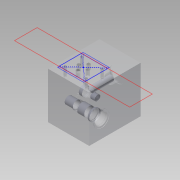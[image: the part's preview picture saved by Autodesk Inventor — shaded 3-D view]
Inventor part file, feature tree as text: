
AUTODESK INVENTOR PART (.ipt)
format: ipt  version: 2014 (Build 180170000, 170)  size: 423,424 bytes
history: native  units: mm
features: other x63, sketch x14, extrude x1
ambient origin geometry x8: Origin, YZ Plane, XZ Plane, XY Plane, X Axis, Y Axis, Z Axis, Center Point
bodies: 实体1 (feature_tree)
feature tree (78):
  other  "NULLNET"
  extrude  "拉伸1"  TaperAngle=0.0deg  [1 undecoded]
  other  "UCS1"
  other  "UCS2"
  other  "UCS3"
  other  "UCS4"
  other  "UCS5"
  other  "UCS6"
  other  "Footprint1"
  other  "Outline1"
  sketch  "草图1"  dims[d0=90.0mm d1=0.0mm]
  sketch  "草图5"  dims[d14=0.0mm d15=0.0mm d16=0.0mm d17=0.0mm d18=0.0mm d19=0.0mm]
  other  "曲面1"
  sketch  "草图6"  dims[d20=0.0mm d21=0.0mm d22=0.0mm d23=0.0mm d24=0.0mm d25=0.0mm]
  other  "曲面2"
  sketch  "草图7"  dims[d26=0.0mm d27=0.0mm d28=0.0mm d29=0.0mm d30=0.0mm d31=0.0mm]
  other  "曲面3"
  sketch  "草图8"  dims[d32=0.0mm d33=0.0mm d34=0.0mm d35=0.0mm d36=0.0mm d37=0.0mm d38=0.0mm]
  other  "曲面4"
  sketch  "草图10"  dims[d56=-48.42mm]
  other  "曲面5"
  sketch  "草图11"  dims[d57=15.87mm d58=0.0mm]
  other  "曲面6"
  sketch  "草图12"  dims[d59=0.13mm d60=-10.297443mm]
  other  "曲面7"
  sketch  "草图14"  dims[d62=13.5mm d63=0.0mm]
  other  "曲面8"
  sketch  "草图15"  dims[d64=-14.359mm d65=3.18mm d66=0.0mm d67=0.0mm d71=-30.09mm d72=8.8mm d73=0.0mm d74=0.13mm d75=-10.297443mm d76=-14.359mm d77=6.35mm d78=0.0mm d79=0.0mm d83=-13.99mm d84=38.81mm d85=0.0mm d86=0.13mm d87=-10.297443mm]
  other  "曲面9"
  other  "2-1cone"
  other  "3-1cone"
  other  "4-1cone"
  other  "UCS1: YZ 平面"
  other  "UCS1: XZ 平面"
  other  "UCS1: XY 平面"
  other  "UCS1: X 轴"
  other  "UCS1: Y 轴"
  other  "UCS1: Z 轴"
  other  "UCS1: 原点"
  other  "UCS2: YZ 平面"
  other  "UCS2: XZ 平面"
  other  "UCS2: XY 平面"
  other  "UCS2: X 轴"
  other  "UCS2: Y 轴"
  other  "UCS2: Z 轴"
  other  "UCS2: 原点"
  other  "UCS3: YZ 平面"
  other  "UCS3: XZ 平面"
  other  "UCS3: XY 平面"
  other  "UCS3: X 轴"
  other  "UCS3: Y 轴"
  other  "UCS3: Z 轴"
  other  "UCS3: 原点"
  other  "UCS4: YZ 平面"
  other  "UCS4: XZ 平面"
  other  "UCS4: XY 平面"
  other  "UCS4: X 轴"
  other  "UCS4: Y 轴"
  other  "UCS4: Z 轴"
  other  "UCS4: 原点"
  other  "UCS5: YZ 平面"
  other  "UCS5: XZ 平面"
  other  "UCS5: XY 平面"
  other  "UCS5: X 轴"
  other  "UCS5: Y 轴"
  other  "UCS5: Z 轴"
  other  "UCS5: 原点"
  other  "UCS6: YZ 平面"
  other  "UCS6: XZ 平面"
  other  "UCS6: XY 平面"
  other  "UCS6: X 轴"
  other  "UCS6: Y 轴"
  other  "UCS6: Z 轴"
  other  "UCS6: 原点"
  sketch  "草图2"  dims[d2=0.0mm d3=0.0mm d4=0.0mm d5=0.0mm d6=0.0mm d7=0.0mm]
  sketch  "草图4"  dims[d8=0.0mm d9=0.0mm d10=0.0mm d11=0.0mm d12=0.0mm d13=0.0mm]
  sketch  "草图9"  dims[d52=0.0mm]
  sketch  "草图13"  dims[d61=-31.039mm]
note: 1 required parameter value undecoded (feature->parameter linkage not recoverable at this tier; creation-order binding heuristic only, values carry confidence <= 0.55)
